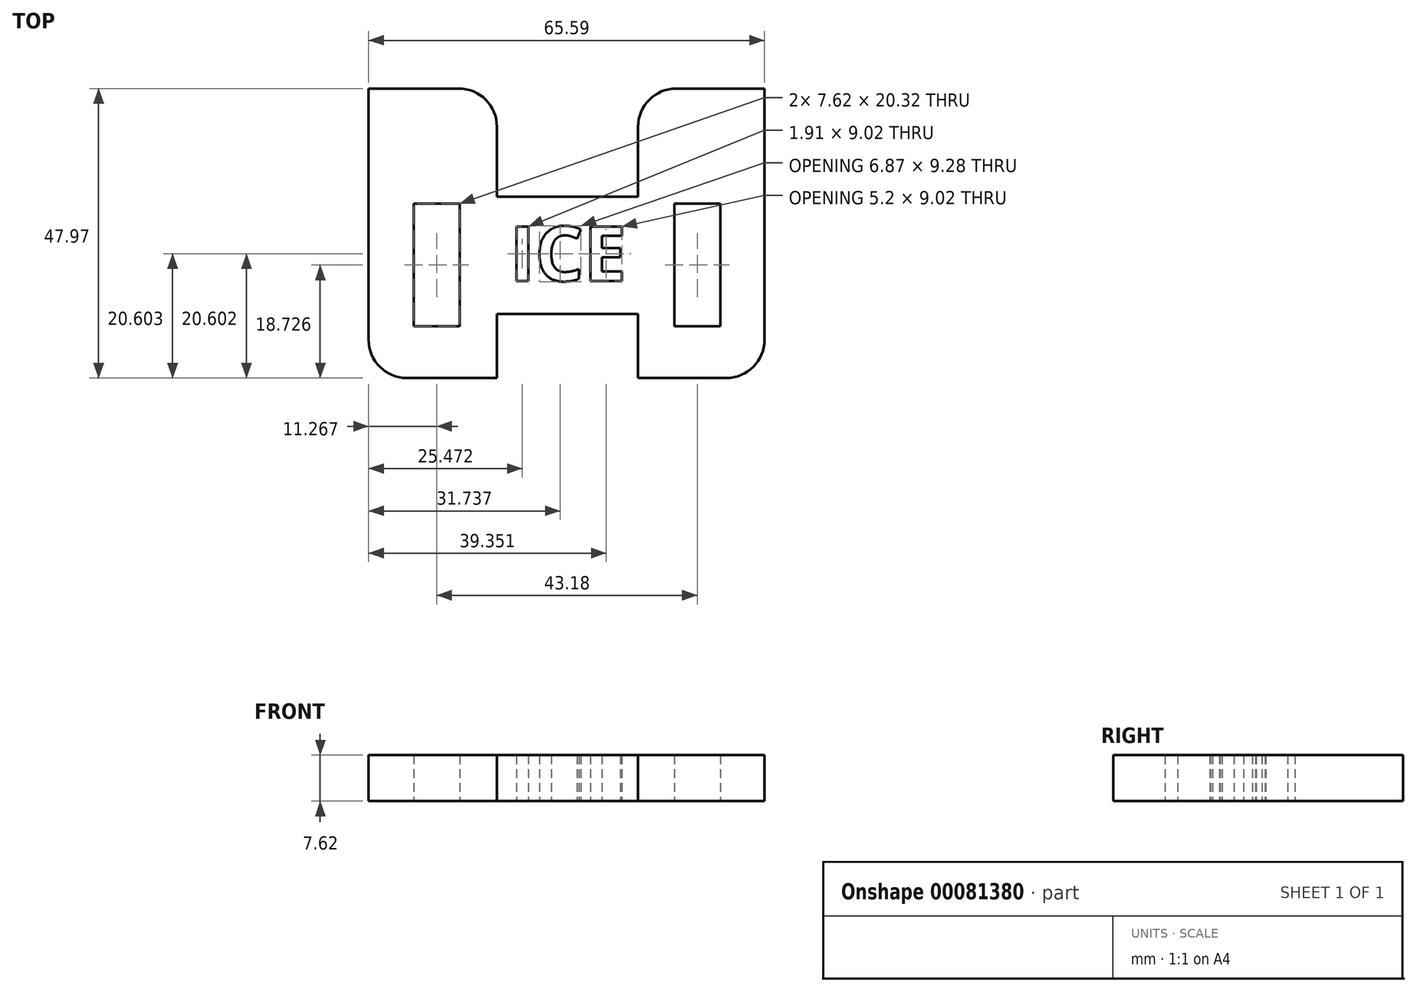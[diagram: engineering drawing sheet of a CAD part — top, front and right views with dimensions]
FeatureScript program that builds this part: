
annotation { "Feature Type Name" : "Feature", "Feature Type Description" : "" }
export const myFeature = defineFeature(function(context is Context, id is Id, definition is map)
    precondition{}
    {
        {
            var Q0;
            Q0=qCreatedBy(makeId("Top.planeOp"),FACE);
            var sketch = newSketch(context, id + "F0", { "sketchPlane" : qUnion([Q0])});
            skLineSegment(sketch, "E0.bottom", {"start": v(-33, 6.88) * mm, "end": v(-25.37, 6.88) * mm});
            skLineSegment(sketch, "E0.top", {"start": v(-33, -13.44) * mm, "end": v(-25.37, -13.44) * mm});
            skLineSegment(sketch, "E0.left", {"start": v(-33, 6.88) * mm, "end": v(-33, -13.44) * mm});
            skLineSegment(sketch, "E0.right", {"start": v(-25.37, 6.88) * mm, "end": v(-25.37, -13.44) * mm});
            skLineSegment(sketch, "E1.bottom", {"start": v(10.19, 6.88) * mm, "end": v(17.8, 6.88) * mm});
            skLineSegment(sketch, "E1.top", {"start": v(10.19, -13.44) * mm, "end": v(17.8, -13.44) * mm});
            skLineSegment(sketch, "E1.left", {"start": v(10.19, 6.88) * mm, "end": v(10.19, -13.44) * mm});
            skLineSegment(sketch, "E1.right", {"start": v(17.8, 6.88) * mm, "end": v(17.8, -13.44) * mm});
            skLineSegment(sketch, "E2.bottom", {"start": v(-40.45, 25.96) * mm, "end": v(-25.55, 25.96) * mm});
            skLineSegment(sketch, "E2.top", {"start": v(-34.1, -22.01) * mm, "end": v(-19.2, -22.01) * mm});
            skLineSegment(sketch, "E2.left", {"start": v(-40.45, 25.96) * mm, "end": v(-40.45, -15.66) * mm});
            skLineSegment(sketch, "E2.right", {"start": v(25.14, 25.96) * mm, "end": v(25.14, -15.66) * mm});
            skLineSegment(sketch, "E3.top", {"start": v(-19.2, -11.39) * mm, "end": v(4.19, -11.39) * mm});
            skLineSegment(sketch, "E3.left", {"start": v(-19.2, -22.01) * mm, "end": v(-19.2, -11.39) * mm});
            skLineSegment(sketch, "E3.right", {"start": v(4.19, -22.01) * mm, "end": v(4.19, -11.39) * mm});
            skLineSegment(sketch, "E4.top", {"start": v(4.19, 8.05) * mm, "end": v(-19.2, 8.05) * mm});
            skLineSegment(sketch, "E4.left", {"start": v(4.19, 19.61) * mm, "end": v(4.19, 8.05) * mm});
            skLineSegment(sketch, "E4.right", {"start": v(-19.2, 19.61) * mm, "end": v(-19.2, 8.05) * mm});
            skLineSegment(sketch, "E5.trimOffspring", {"start": v(10.54, 25.96) * mm, "end": v(25.14, 25.96) * mm});
            skLineSegment(sketch, "E6.trimOffspring", {"start": v(4.19, -22.01) * mm, "end": v(18.8, -22.01) * mm});
            skPoint(sketch, "E7.visualSharp", {"position": v(-19.2, 25.96) * mm});
            skArc(sketch, "E7.filletArc", {"start": v(-19.2, 19.61) * mm, "mid": v(-21.06, 24.1) * mm, "end": v(-25.55, 25.96) * mm});
            skPoint(sketch, "E8.visualSharp", {"position": v(4.19, 25.96) * mm});
            skArc(sketch, "E8.filletArc", {"start": v(10.54, 25.96) * mm, "mid": v(6.05, 24.1) * mm, "end": v(4.19, 19.61) * mm});
            skPoint(sketch, "E9.visualSharp", {"position": v(25.14, -22.01) * mm});
            skArc(sketch, "E9.filletArc", {"start": v(18.8, -22.01) * mm, "mid": v(23.28, -20.15) * mm, "end": v(25.14, -15.66) * mm});
            skPoint(sketch, "E10.visualSharp", {"position": v(-40.45, -22.01) * mm});
            skArc(sketch, "E10.filletArc", {"start": v(-40.45, -15.66) * mm, "mid": v(-38.6, -20.15) * mm, "end": v(-34.1, -22.01) * mm});
            skText(sketch, "E11", { "text": "ICE", "fontName": "OpenSans-Bold.ttf"});
            const initialGuessF0  = {"E11": [-0.01707, -0.00592, 1, 0, 0.0091]};
            skSetInitialGuess(sketch, initialGuessF0);
            skSolve(sketch);
        }
        {
            var Q0;
            Q0 = qSketchRegion(id + "F0", true);
            extrude(context, id + "F1", {"entities" : qUnion([Q0]), "depth" : 7.62 * mm});
        }
    });
